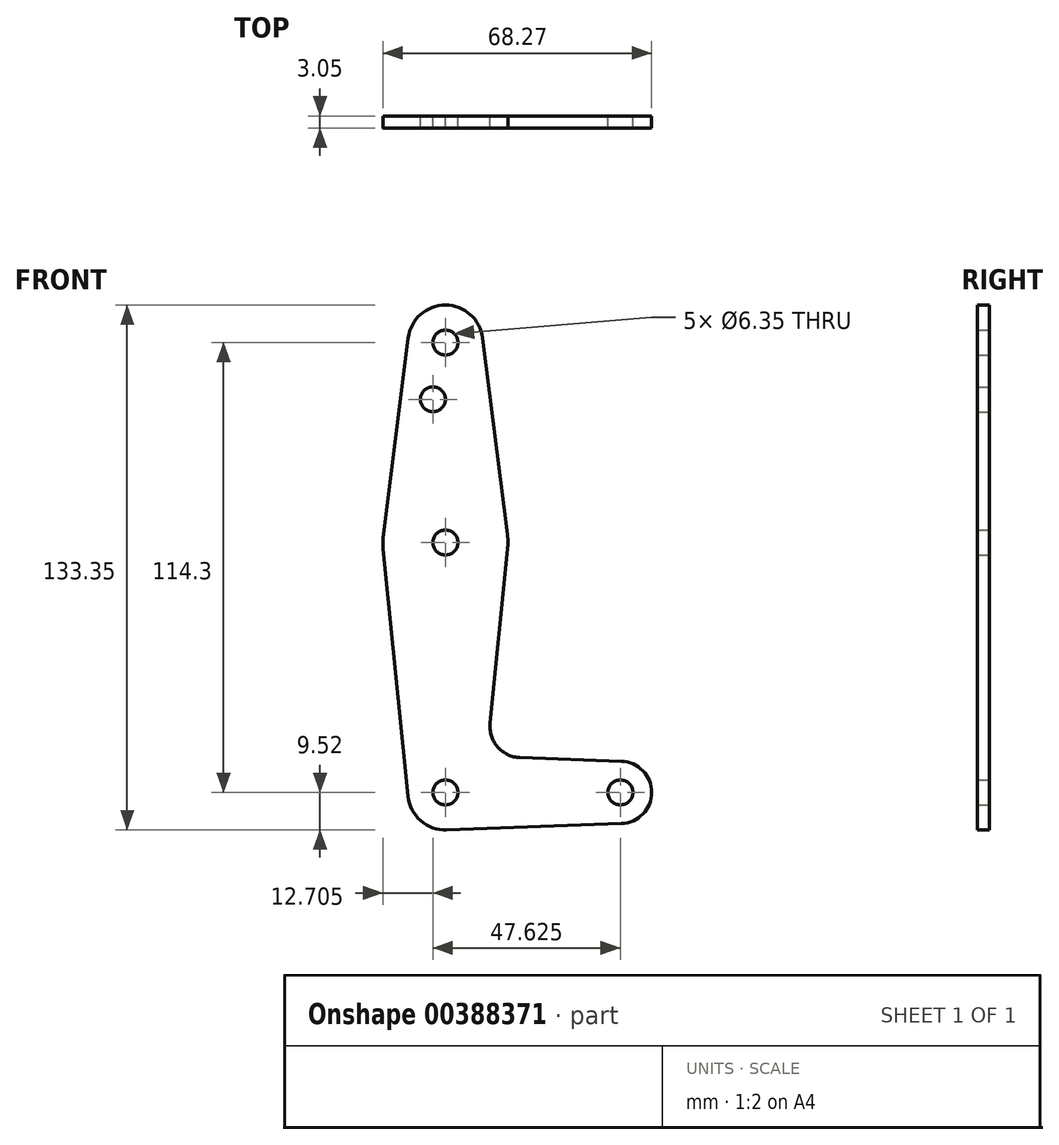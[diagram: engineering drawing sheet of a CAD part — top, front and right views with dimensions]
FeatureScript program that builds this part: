
annotation { "Feature Type Name" : "Feature", "Feature Type Description" : "" }
export const myFeature = defineFeature(function(context is Context, id is Id, definition is map)
    precondition{}
    {
        {
            var Q0;
            Q0=qCreatedBy(makeId("Front.planeOp"),FACE);
            var sketch = newSketch(context, id + "F0", { "sketchPlane" : qUnion([Q0])});
            skLineSegment(sketch, "E0", {"start": v(0, 114.3) * mm, "end": v(0, 0) * mm, "construction": true});
            skLineSegment(sketch, "E1", {"start": v(0, 0) * mm, "end": v(44.45, 0) * mm, "construction": true});
            skCircle(sketch, "E2", {"center": v(0, 0) * mm, "radius": 9.53 * mm});
            skCircle(sketch, "E3", {"center": v(0, 63.5) * mm, "radius": 15.88 * mm});
            skCircle(sketch, "E4", {"center": v(0, 114.3) * mm, "radius": 9.53 * mm});
            skCircle(sketch, "E5", {"center": v(44.45, 0) * mm, "radius": 7.94 * mm});
            skLineSegment(sketch, "E6", {"start": v(-9.45, 115.5) * mm, "end": v(-15.75, 65.48) * mm});
            skLineSegment(sketch, "E7", {"start": v(-15.8, 61.91) * mm, "end": v(-9.48, -0.95) * mm});
            skLineSegment(sketch, "E8", {"start": v(9.45, 115.5) * mm, "end": v(15.75, 65.48) * mm});
            skLineSegment(sketch, "E9", {"start": v(15.8, 61.91) * mm, "end": v(11.34, 17.6) * mm});
            skLineSegment(sketch, "E10", {"start": v(0.34, -9.52) * mm, "end": v(44.73, -7.93) * mm});
            skLineSegment(sketch, "E11", {"start": v(18.97, 8.85) * mm, "end": v(44.73, 7.93) * mm});
            skCircle(sketch, "E12", {"center": v(0, 114.3) * mm, "radius": 3.18 * mm});
            skCircle(sketch, "E13", {"center": v(0, 63.5) * mm, "radius": 3.18 * mm});
            skCircle(sketch, "E14", {"center": v(0, 0) * mm, "radius": 3.18 * mm});
            skCircle(sketch, "E15", {"center": v(44.45, 0) * mm, "radius": 3.18 * mm});
            skCircle(sketch, "E16", {"center": v(-3.17, 99.89) * mm, "radius": 3.18 * mm});
            skArc(sketch, "E17.filletArc", {"start": v(11.34, 17.6) * mm, "mid": v(13.26, 11.57) * mm, "end": v(18.97, 8.85) * mm});
            skSolve(sketch);
        }
        {
            var Q0;
            Q0 = qSketchRegion(id + "F0", true);
            extrude(context, id + "F1", {"entities" : qUnion([Q0]), "depth" : 3.05 * mm});
        }
    });
